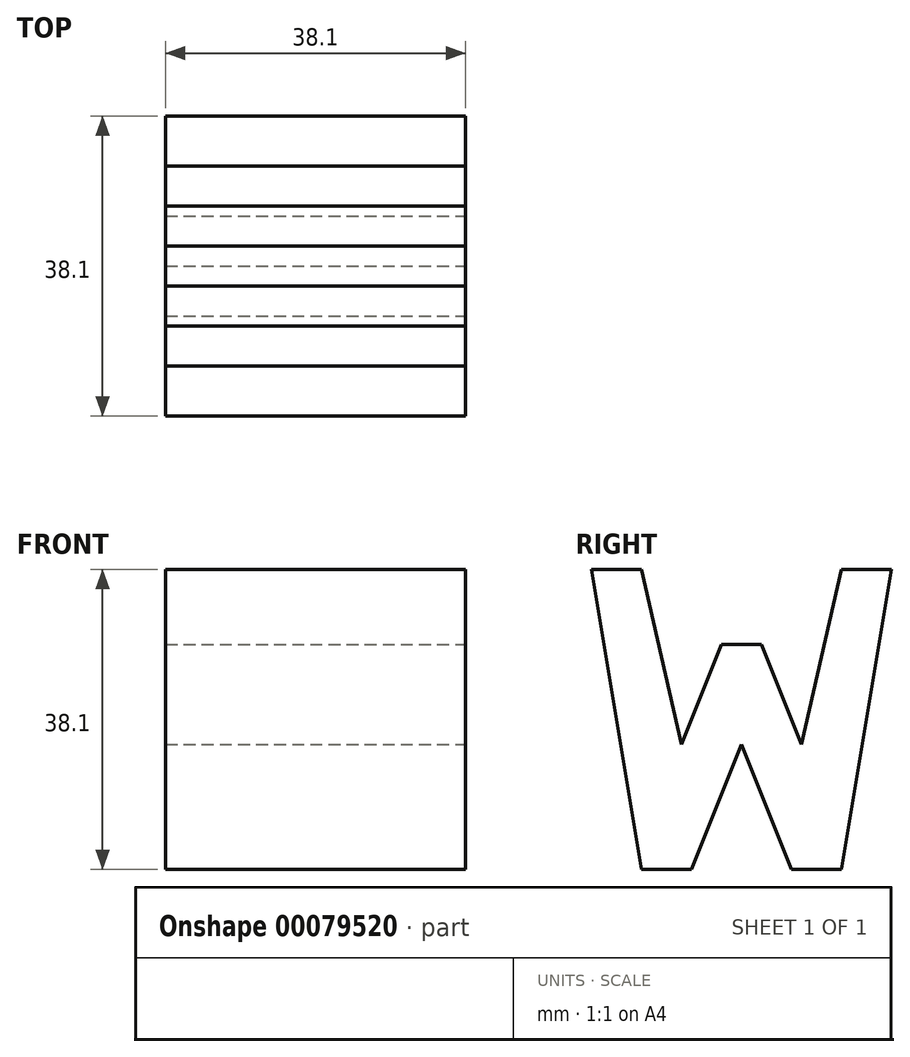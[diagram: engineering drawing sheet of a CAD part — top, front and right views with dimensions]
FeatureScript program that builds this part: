
annotation { "Feature Type Name" : "Feature", "Feature Type Description" : "" }
export const myFeature = defineFeature(function(context is Context, id is Id, definition is map)
    precondition{}
    {
        {
            var Q0;
            Q0=qCreatedBy(makeId("Front.planeOp"),FACE);
            var sketch = newSketch(context, id + "F0", { "sketchPlane" : qUnion([Q0])});
            skLineSegment(sketch, "E0", {"start": v(0, 0) * mm, "end": v(38.1, 0) * mm});
            skLineSegment(sketch, "E1", {"start": v(0, 0) * mm, "end": v(0, 38.1) * mm});
            skLineSegment(sketch, "E2", {"start": v(0, 38.1) * mm, "end": v(38.1, 38.1) * mm});
            skLineSegment(sketch, "E3", {"start": v(38.1, 38.1) * mm, "end": v(38.1, 0) * mm});
            skSolve(sketch);
        }
        {
            var Q0;
            Q0=makeQuery(id+"F0.imprint","IMPRINT",FACE,{"disambiguationData":[TD([[makeQuery(id+"F0.imprint","IMPRINT",EDGE,{"derivedFrom":sQuery(id+"F0.wireOp",EDGE,"E0")}),1.0]])]});
            extrude(context, id + "F1", {"entities" : qUnion([Q0]), "depth" : 38.1 * mm});
        }
        {
            var Q0;
            Q0=qCreatedBy(makeId("Right.planeOp"),FACE);
            cPlane(context, id + "F2", {"entities" : qUnion([Q0]), "cplaneType" : CPlaneType.OFFSET, "offset" : 38.1 * mm, "width" : 152.4 * mm, "height" : 152.4 * mm});
        }
        {
            var Q0;
            Q0=qCreatedBy(id+"F2.planeOp",FACE);
            var sketch = newSketch(context, id + "F3", { "sketchPlane" : qUnion([Q0])});
            skLineSegment(sketch, "E4.bottom", {"start": v(-38.1, 38.1) * mm, "end": v(0, 38.1) * mm});
            skLineSegment(sketch, "E4.top", {"start": v(-38.1, 0) * mm, "end": v(0, 0) * mm});
            skLineSegment(sketch, "E4.left", {"start": v(-38.1, 38.1) * mm, "end": v(-38.1, 0) * mm});
            skLineSegment(sketch, "E4.right", {"start": v(0, 38.1) * mm, "end": v(0, 0) * mm});
            skLineSegment(sketch, "E5", {"start": v(-38.1, 38.1) * mm, "end": v(-31.75, 0) * mm});
            skPoint(sketch, "E6.endSnap0", {"position": v(-34.92, 19.05) * mm});
            skLineSegment(sketch, "E7", {"start": v(-6.35, 0) * mm, "end": v(0, 38.1) * mm});
            skLineSegment(sketch, "E8", {"start": v(-25.4, 0) * mm, "end": v(-19.05, 15.88) * mm});
            skPoint(sketch, "E8.endSnap0", {"position": v(-19.05, 0) * mm});
            skLineSegment(sketch, "E9", {"start": v(-19.05, 15.88) * mm, "end": v(-12.7, 0) * mm});
            skLineSegment(sketch, "E10", {"start": v(-26.67, 15.88) * mm, "end": v(-21.6, 28.58) * mm});
            skLineSegment(sketch, "E11", {"start": v(-21.6, 28.58) * mm, "end": v(-16.51, 28.58) * mm});
            skLineSegment(sketch, "E12", {"start": v(-26.67, 15.87) * mm, "end": v(-31.75, 38.1) * mm});
            skLineSegment(sketch, "E13", {"start": v(-16.51, 28.58) * mm, "end": v(-11.43, 15.88) * mm});
            skLineSegment(sketch, "E14", {"start": v(-11.43, 15.88) * mm, "end": v(-6.35, 38.1) * mm});
            skSolve(sketch);
        }
        {
            var Q0;
            Q0=makeQuery(id+"F3.imprint","IMPRINT",FACE,{"disambiguationData":[TD([[makeQuery(id+"F3.imprint","IMPRINT",EDGE,{"derivedFrom":sQuery(id+"F3.wireOp",EDGE,"E10")}),1.0]])]});
            var Q1;
            {var subQ0=sQuery(id+"F3.wireOp",EDGE,"E4.left");Q1=makeQuery(id+"F3.imprint","IMPRINT",FACE,{"disambiguationData":[TD([[makeQuery(id+"F3.imprint","IMPRINT",EDGE,{"derivedFrom":subQ0}),1.0]])]});}
            var Q2;
            {var subQ0=sQuery(id+"F3.wireOp",EDGE,"E8");Q2=makeQuery(id+"F3.imprint","IMPRINT",FACE,{"disambiguationData":[TD([[makeQuery(id+"F3.imprint","IMPRINT",EDGE,{"derivedFrom":subQ0}),-1.0]])]});}
            var Q3;
            {var subQ0=sQuery(id+"F3.wireOp",EDGE,"E4.right");Q3=makeQuery(id+"F3.imprint","IMPRINT",FACE,{"disambiguationData":[TD([[makeQuery(id+"F3.imprint","IMPRINT",EDGE,{"derivedFrom":subQ0}),-1.0]])]});}
            extrude(context, id + "F4", {"entities" : qUnion([Q0, Q1, Q2, Q3]), "operationType" : NewBodyOperationType.REMOVE, "oppositeDirection" : true, "depth" : 38.1 * mm});
        }
    });
